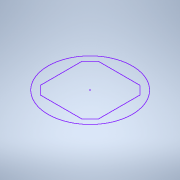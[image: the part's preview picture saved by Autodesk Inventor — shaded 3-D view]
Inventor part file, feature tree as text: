
AUTODESK INVENTOR PART (.ipt)
format: ipt  version: 2021 (Build 250183000, 183)  size: 87,552 bytes
history: native  units: mm
features: sketch x1
ambient origin geometry x8: Origin, YZ Plane, XZ Plane, XY Plane, X Axis, Y Axis, Z Axis, Center Point
feature tree (1):
  sketch  "Boceto1"
